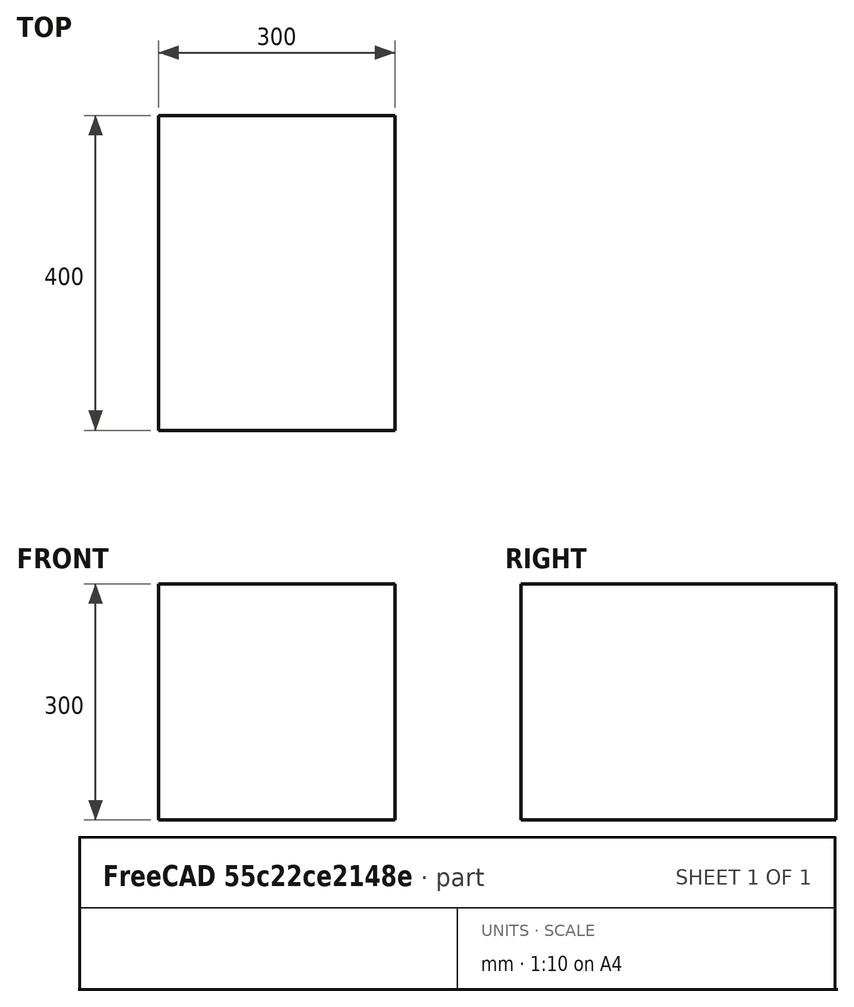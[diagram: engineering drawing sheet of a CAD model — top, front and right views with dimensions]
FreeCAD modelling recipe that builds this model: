
FCSTD DOCUMENT  (FreeCAD 0.16R6706 (Git))
Label: min_printing_volume
License: All rights reserved
LicenseURL: http://en.wikipedia.org/wiki/All_rights_reserved
objects: Part::Box×1, Drawing::FeatureViewPart×1, Drawing::FeaturePage×1
note: 1 computed .brp shape members not serialized (recipe doc carries the construction recipe); baked Part::Feature solids carry a one-line shape summary decoded from their .brp

FEATURE [Part::Box] Box  label="Cube"
  Height = 300
  Length = 300
  Width = 400
FEATURE [Drawing::FeatureViewPart] View
  Direction = (1,-1,1)
  HiddenWidth = 0.15
  LineWidth = 0.35
  Rotation = 60
  Scale = 0.1
  ShowHiddenLines = true
  ShowSmoothLines = false
  Source = -> Box
  Tolerance = 0.05
  ViewResult = <g id="View"\n   transform="rotate(60,80.2513,162.789) translate(80.2513,162.789) scale(0.1,0.1)"\n  >\n<g   stroke="rgb(0, 0, 0)"\n   stroke-width="1.5"\n   stroke-linecap="butt"\n   stroke-linejoin="miter"\n   stroke-dasharray="0.2,0.1"\n   fill="none"\n   transform="scale(1,-1)"\n  >\n<path id= "1" d=" M 0 326.599 L -212.132 449.073 " />\n<path id= "2" d=" M 0 0 L 0 326.599 " />\n<path id= "3" d=" M 0 326.599 L 212.132 449.073 " />\n</g>\n<g   stroke="rgb(0, 0, 0)"\n   stroke-width="3.5"\n   stroke-linecap="butt"\n   stroke-linejoin="miter"\n   fill="none"\n   transform="scale(1,-1)"\n  >\n<path id= "1" d=" M 0 0 L -212.132 122.474 " />\n<path id= "2" d=" M -212.132 122.474 L -212.132 449.073 " />\n<path id= "3" d=" M 212.132 122.474 L -2.84217e-14 244.949 " />\n<path id= "4" d=" M 0 244.949 L 0 571.548 " />\n<path id= "5" d=" M 212.132 449.073 L -2.84217e-14 571.548 " />\n<path id= "6" d=" M 212.132 122.474 L 212.132 449.073 " />\n<path id= "7" d=" M 0 0 L 212.132 122.474 " />\n<path id= "8" d=" M -212.132 122.474 L 2.84217e-14 244.949 " />\n<path id= "9" d=" M -212.132 449.073 L 2.84217e-14 571.548 " />\n</g>\n</g>
  Visible = true
  X = 80.2513
  Y = 162.789
FEATURE [Drawing::FeaturePage] Page
  Group = -> [View]
